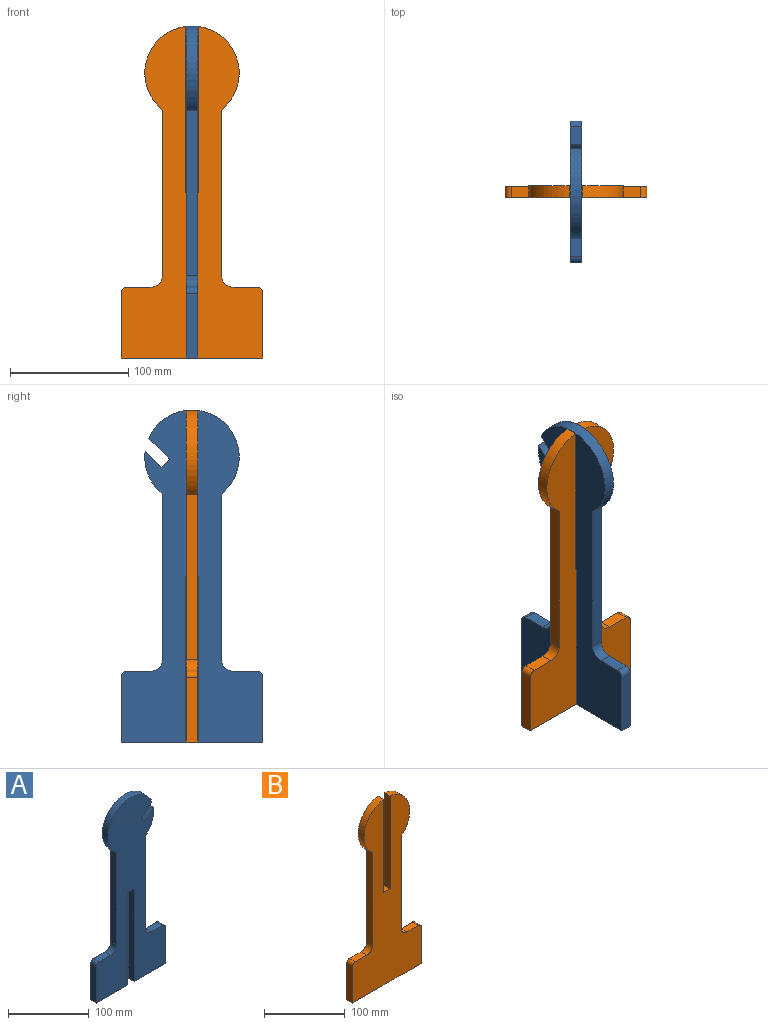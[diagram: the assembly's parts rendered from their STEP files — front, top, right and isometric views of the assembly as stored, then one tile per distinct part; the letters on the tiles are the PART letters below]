
ASSEMBLY  parts=2 mates=1
PART A: 22 faces, bbox 120x10x281.2 mm
  f0: cylinder r=40mm len=76.63mm, axis (0,1,0), area 1449.4mm2, adj f1,f19,f20,f21
  f1: plane 140x10mm, normal (-1,0,0), area 1400mm2, adj f0,f2,f20,f21
  f2: cylinder r=10mm len=10mm, axis (0,1,0), area 157.1mm2, adj f1,f3,f20,f21
  f3: plane 20x10mm, normal (0,0,1), area 200mm2, adj f2,f4,f20,f21
  f4: cylinder r=5mm len=10mm, axis (0,1,0), area 78.5mm2, adj f3,f5,f20,f21
  f5: plane 55x10mm, normal (-1,0,0), area 550mm2, adj f4,f6,f20,f21
  f6: plane 54.5x10mm, normal (0,0,-1), area 545mm2, adj f5,f7,f20,f21
  f7: plane 140x10mm, normal (1,0,0), area 1400mm2, adj f6,f8,f20,f21
  f8: plane 11x10mm, normal (0,0,-1), area 110mm2, adj f7,f9,f20,f21
  f9: plane 140x10mm, normal (-1,0,0), area 1400mm2, adj f8,f10,f20,f21
  f10: plane 54.5x10mm, normal (0,0,-1), area 545mm2, adj f9,f11,f20,f21
  f11: plane 55x10mm, normal (1,0,0), area 550mm2, adj f10,f12,f20,f21
  f12: cylinder r=5mm len=10mm, axis (0,1,0), area 78.5mm2, adj f11,f13,f20,f21
  f13: plane 20x10mm, normal (0,0,1), area 200mm2, adj f12,f14,f20,f21
  f14: cylinder r=10mm len=10mm, axis (0,1,0), area 157.1mm2, adj f13,f15,f20,f21
  f15: plane 140x10mm, normal (1,0,0), area 1400mm2, adj f14,f16,f20,f21
  f16: cylinder r=40mm len=36.23mm, axis (0,1,0), area 408.4mm2, adj f15,f17,f20,f21
  f17: plane 13.67x13.67mm, normal (-0.71,0,0.71), area 193.3mm2, adj f16,f18,f20,f21
  f18: plane 10x7.07mm, normal (0.71,0,0.71), area 100mm2, adj f17,f19,f20,f21
  f19: plane 17.68x17.68mm, normal (0.71,0,-0.71), area 250mm2, adj f0,f18,f20,f21
  f20: plane 281.23x120mm, normal (0,-1,0), area 17694.3mm2, adj f0,f1,f2,f3,f4,f5,f6,f7
  f21: plane 281.23x120mm, normal (0,1,0), area 17694.3mm2, adj f0,f1,f2,f3,f4,f5,f6,f7
PART B: 18 faces, bbox 120x10x280.8 mm
  f0: plane 140x10mm, normal (1,0,0), area 1400mm2, adj f1,f15,f16,f17
  f1: cylinder r=40mm len=70.85mm, axis (0,-1,0), area 931.4mm2, adj f0,f2,f16,f17
  f2: plane 140.85x10mm, normal (-1,0,0), area 1408.5mm2, adj f1,f3,f16,f17
  f3: plane 11x10mm, normal (0,0,1), area 110mm2, adj f2,f4,f16,f17
  f4: plane 140.85x10mm, normal (1,0,0), area 1408.5mm2, adj f3,f5,f16,f17
  f5: cylinder r=40mm len=70.85mm, axis (0,-1,0), area 931.4mm2, adj f4,f6,f16,f17
  f6: plane 140x10mm, normal (-1,0,0), area 1400mm2, adj f5,f7,f16,f17
  f7: cylinder r=10mm len=10mm, axis (0,-1,0), area 157.1mm2, adj f6,f8,f16,f17
  f8: plane 20x10mm, normal (0,0,1), area 200mm2, adj f7,f9,f16,f17
  f9: cylinder r=5mm len=10mm, axis (0,-1,0), area 78.5mm2, adj f8,f10,f16,f17
  f10: plane 55x10mm, normal (-1,0,0), area 550mm2, adj f9,f11,f16,f17
  f11: plane 120x10mm, normal (0,0,-1), area 1200mm2, adj f10,f12,f16,f17
  f12: plane 55x10mm, normal (1,0,0), area 550mm2, adj f11,f13,f16,f17
  f13: cylinder r=5mm len=10mm, axis (0,-1,0), area 78.5mm2, adj f12,f14,f16,f17
  f14: plane 20x10mm, normal (0,0,1), area 200mm2, adj f13,f15,f16,f17
  f15: cylinder r=10mm len=10mm, axis (0,-1,0), area 157.1mm2, adj f0,f14,f16,f17
  f16: plane 280.85x120mm, normal (0,1,0), area 17907.1mm2, adj f0,f1,f2,f3,f4,f5,f6,f7
  f17: plane 280.85x120mm, normal (0,-1,0), area 17907.1mm2, adj f0,f1,f2,f3,f4,f5,f6,f7
PLACE A rot(axis=(0,0,1),90deg) t=(-5,5,0)mm
PLACE B at identity
MATE fastened A.f8 <-> B.f3  axis (0,0,-1) through (0,5,-101.22)mm
